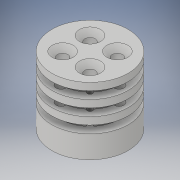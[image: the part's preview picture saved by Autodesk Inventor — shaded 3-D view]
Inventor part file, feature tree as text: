
AUTODESK INVENTOR PART (.ipt)
format: ipt  version: 2019 (Build 230136000, 136)  size: 311,296 bytes
history: native  units: mm
features: sketch x8, extrude x6, other x3, revolve x1, hole x1
ambient origin geometry x8: Origin, YZ Plane, XZ Plane, XY Plane, X Axis, Y Axis, Z Axis, Center Point
bodies: Body1 (feature_tree)
feature tree (19):
  other  "Bryła1"
  extrude  "Wyciągnięcie proste1"  Depth=20.0mm
  other  "Płaszczyzna konstrukcyjna1"
  revolve  "Obrót1"
  extrude  "Wyciągnięcie proste6"  Depth=25.0mm
  extrude  "Wyciągnięcie proste7"  Depth=5.0mm TaperAngle=0.0deg
  extrude  "Wyciągnięcie proste8"  Depth=2.5mm
  other  "Płaszczyzna konstrukcyjna2"
  extrude  "Wyciągnięcie proste9"  Depth=22.0mm
  extrude  "Wyciągnięcie proste10"  Depth=3.0mm
  hole  "Otwór1"  [1 undecoded]
  sketch  "Szkic1"
  sketch  "Szkic5"
  sketch  "Szkic7"
  sketch  "Szkic8"
  sketch  "Szkic9"
  sketch  "Szkic10"
  sketch  "Szkic11"
  sketch  "Szkic12"
note: 1 required parameter value undecoded (feature->parameter linkage not recoverable at this tier; creation-order binding heuristic only, values carry confidence <= 0.55)
